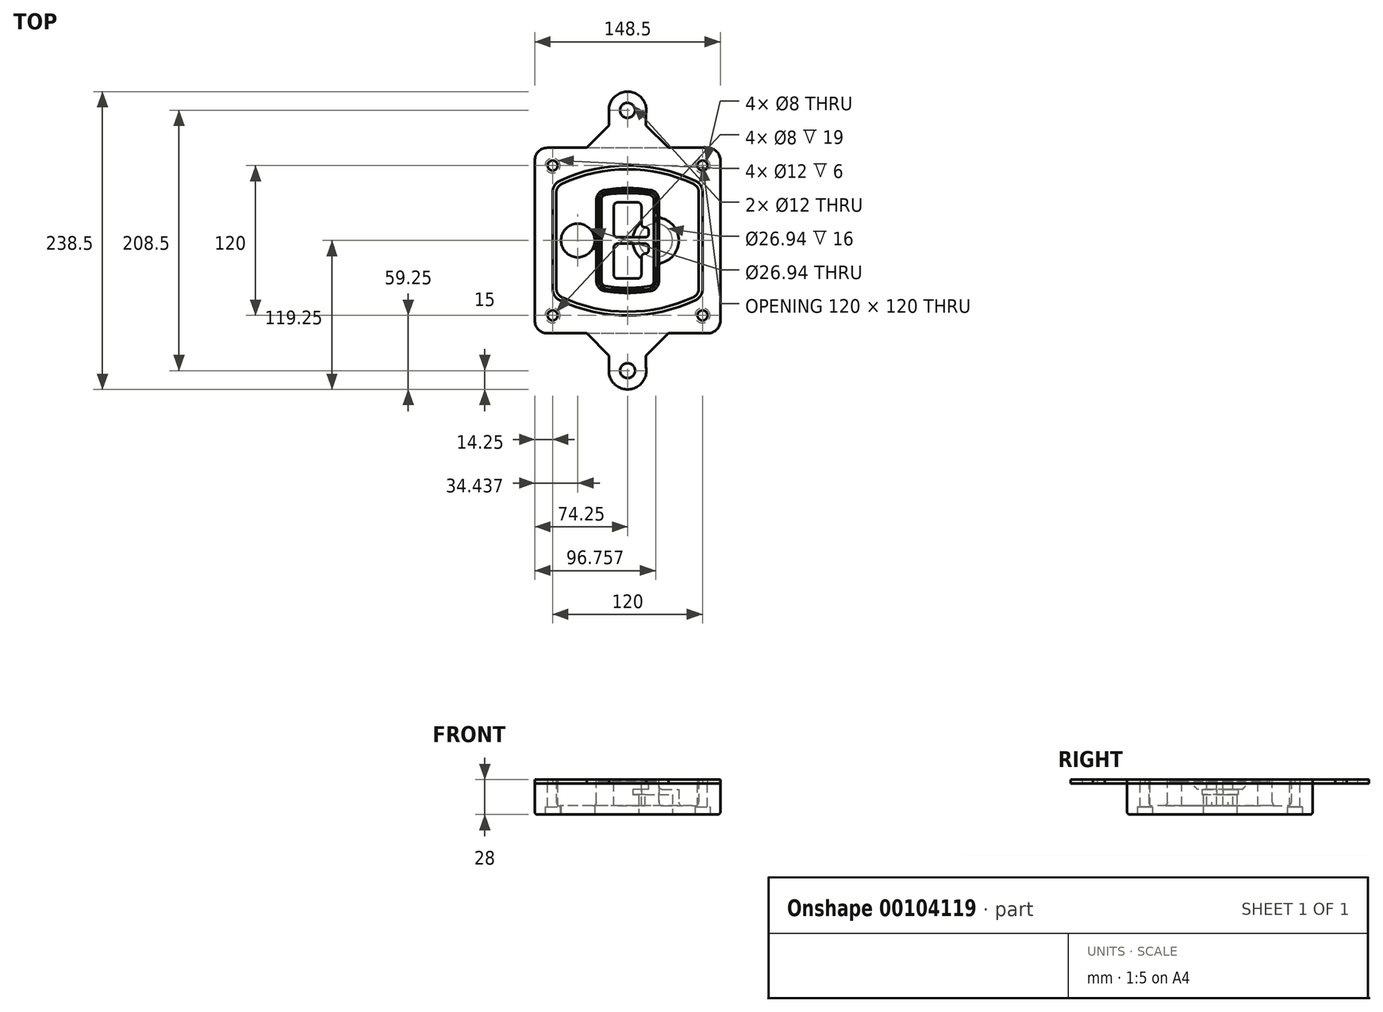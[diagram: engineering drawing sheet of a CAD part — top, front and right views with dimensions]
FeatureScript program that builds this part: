
annotation { "Feature Type Name" : "Feature", "Feature Type Description" : "" }
export const myFeature = defineFeature(function(context is Context, id is Id, definition is map)
    precondition{}
    {
        {
            var Q0;
            Q0=qCreatedBy(makeId("Top.planeOp"),FACE);
            var sketch = newSketch(context, id + "F0", { "sketchPlane" : qUnion([Q0])});
            skPoint(sketch, "E0.rect.middle", {"position": v(0, 0) * mm});
            skLineSegment(sketch, "E1.bottom", {"start": v(-64.25, -74.25) * mm, "end": v(64.25, -74.25) * mm});
            skLineSegment(sketch, "E1.top", {"start": v(-64.25, 74.25) * mm, "end": v(64.25, 74.25) * mm});
            skLineSegment(sketch, "E1.left", {"start": v(-74.25, -64.25) * mm, "end": v(-74.25, 64.25) * mm});
            skLineSegment(sketch, "E1.right", {"start": v(74.25, -64.25) * mm, "end": v(74.25, 64.25) * mm});
            skLineSegment(sketch, "E2", {"start": v(-74.25, 74.25) * mm, "end": v(74.25, -74.25) * mm, "construction": true});
            skLineSegment(sketch, "E3", {"start": v(74.25, 74.25) * mm, "end": v(-74.25, -74.25) * mm, "construction": true});
            skCircle(sketch, "E4", {"center": v(-60, 60) * mm, "radius": 4 * mm});
            skCircle(sketch, "E5", {"center": v(60, 60) * mm, "radius": 4 * mm});
            skCircle(sketch, "E6", {"center": v(60, -60) * mm, "radius": 4 * mm});
            skCircle(sketch, "E7", {"center": v(-60, -60) * mm, "radius": 4 * mm});
            skLineSegment(sketch, "E8", {"start": v(-60, 60) * mm, "end": v(60, 60) * mm, "construction": true});
            skLineSegment(sketch, "E9", {"start": v(60, 60) * mm, "end": v(60, -60) * mm, "construction": true});
            skLineSegment(sketch, "E10", {"start": v(60, -60) * mm, "end": v(-60, -60) * mm, "construction": true});
            skLineSegment(sketch, "E11", {"start": v(-60, -60) * mm, "end": v(-60, 60) * mm, "construction": true});
            skLineSegment(sketch, "E12", {"start": v(-60, 38.83) * mm, "end": v(-60, -38.83) * mm});
            skLineSegment(sketch, "E13", {"start": v(60, 38.83) * mm, "end": v(60, -38.83) * mm});
            skArc(sketch, "E14", {"start": v(54.26, 47.88) * mm, "mid": v(0, 60) * mm, "end": v(-54.26, 47.88) * mm});
            skArc(sketch, "E15", {"start": v(-54.26, -47.88) * mm, "mid": v(0, -60) * mm, "end": v(54.26, -47.88) * mm});
            skLineSegment(sketch, "E16", {"start": v(-60, 0) * mm, "end": v(60, 0) * mm, "construction": true});
            skPoint(sketch, "E17.visualSharp", {"position": v(-60, -45) * mm});
            skArc(sketch, "E17.filletArc", {"start": v(-60, -38.83) * mm, "mid": v(-58.44, -44.2) * mm, "end": v(-54.26, -47.88) * mm});
            skPoint(sketch, "E18.visualSharp", {"position": v(-60, 45) * mm});
            skArc(sketch, "E18.filletArc", {"start": v(-54.26, 47.88) * mm, "mid": v(-58.44, 44.2) * mm, "end": v(-60, 38.83) * mm});
            skPoint(sketch, "E19.visualSharp", {"position": v(60, 45) * mm});
            skArc(sketch, "E19.filletArc", {"start": v(60, 38.83) * mm, "mid": v(58.44, 44.2) * mm, "end": v(54.26, 47.88) * mm});
            skPoint(sketch, "E20.visualSharp", {"position": v(60, -45) * mm});
            skArc(sketch, "E20.filletArc", {"start": v(54.26, -47.88) * mm, "mid": v(58.44, -44.2) * mm, "end": v(60, -38.83) * mm});
            skPoint(sketch, "E21.visualSharp", {"position": v(-74.25, 74.25) * mm});
            skArc(sketch, "E21.filletArc", {"start": v(-64.25, 74.25) * mm, "mid": v(-71.32, 71.32) * mm, "end": v(-74.25, 64.25) * mm});
            skPoint(sketch, "E22.visualSharp", {"position": v(74.25, 74.25) * mm});
            skArc(sketch, "E22.filletArc", {"start": v(74.25, 64.25) * mm, "mid": v(71.32, 71.32) * mm, "end": v(64.25, 74.25) * mm});
            skPoint(sketch, "E23.visualSharp", {"position": v(74.25, -74.25) * mm});
            skArc(sketch, "E23.filletArc", {"start": v(64.25, -74.25) * mm, "mid": v(71.32, -71.32) * mm, "end": v(74.25, -64.25) * mm});
            skPoint(sketch, "E24.visualSharp", {"position": v(-74.25, -74.25) * mm});
            skArc(sketch, "E24.filletArc", {"start": v(-74.25, -64.25) * mm, "mid": v(-71.32, -71.32) * mm, "end": v(-64.25, -74.25) * mm});
            skArc(sketch, "E25.0", {"start": v(57, 38.83) * mm, "mid": v(55.9, 42.58) * mm, "end": v(52.98, 45.17) * mm});
            skLineSegment(sketch, "E25.1", {"start": v(57, 38.83) * mm, "end": v(57, -38.83) * mm});
            skArc(sketch, "E25.2", {"start": v(52.98, -45.17) * mm, "mid": v(55.9, -42.58) * mm, "end": v(57, -38.83) * mm});
            skArc(sketch, "E25.3", {"start": v(-52.98, -45.17) * mm, "mid": v(0, -57) * mm, "end": v(52.98, -45.17) * mm});
            skArc(sketch, "E25.4", {"start": v(-57, -38.83) * mm, "mid": v(-55.9, -42.58) * mm, "end": v(-52.98, -45.17) * mm});
            skArc(sketch, "E25.5", {"start": v(52.98, 45.17) * mm, "mid": v(0, 57) * mm, "end": v(-52.98, 45.17) * mm});
            skLineSegment(sketch, "E25.6", {"start": v(-57, 38.83) * mm, "end": v(-57, -38.83) * mm});
            skArc(sketch, "E25.7", {"start": v(-52.98, 45.17) * mm, "mid": v(-55.9, 42.58) * mm, "end": v(-57, 38.83) * mm});
            skArc(sketch, "E26.0", {"start": v(-55.96, 51.5) * mm, "mid": v(-61.82, 46.33) * mm, "end": v(-64, 38.83) * mm});
            skArc(sketch, "E26.1", {"start": v(55.96, 51.5) * mm, "mid": v(0, 64) * mm, "end": v(-55.96, 51.5) * mm});
            skArc(sketch, "E26.2", {"start": v(64, 38.83) * mm, "mid": v(61.82, 46.33) * mm, "end": v(55.96, 51.5) * mm});
            skLineSegment(sketch, "E26.3", {"start": v(64, 38.83) * mm, "end": v(64, -38.83) * mm});
            skArc(sketch, "E26.4", {"start": v(55.96, -51.5) * mm, "mid": v(61.82, -46.33) * mm, "end": v(64, -38.83) * mm});
            skLineSegment(sketch, "E26.5", {"start": v(-64, 38.83) * mm, "end": v(-64, -38.83) * mm});
            skArc(sketch, "E26.6", {"start": v(-55.96, -51.5) * mm, "mid": v(0, -64) * mm, "end": v(55.96, -51.5) * mm});
            skArc(sketch, "E26.7", {"start": v(-64, -38.83) * mm, "mid": v(-61.82, -46.33) * mm, "end": v(-55.96, -51.5) * mm});
            skSolve(sketch);
        }
        {
            var Q0;
            Q0=makeQuery(id+"F0.imprint","IMPRINT",FACE,{"disambiguationData":[TD([[makeQuery(id+"F0.imprint","IMPRINT",EDGE,{"derivedFrom":sQuery(id+"F0.wireOp",EDGE,"E1.bottom")}),1.0]])]});
            var Q1;
            Q1=makeQuery(id+"F0.imprint","IMPRINT",FACE,{"disambiguationData":[TD([[makeQuery(id+"F0.imprint","IMPRINT",EDGE,{"derivedFrom":sQuery(id+"F0.wireOp",EDGE,"E12")}),1.0]])]});
            var Q2;
            Q2=makeQuery(id+"F0.imprint","IMPRINT",FACE,{"disambiguationData":[TD([[makeQuery(id+"F0.imprint","IMPRINT",EDGE,{"derivedFrom":sQuery(id+"F0.wireOp",EDGE,"E25.0")}),1.0]])]});
            var Q3;
            Q3=makeQuery(id+"F0.imprint","IMPRINT",FACE,{"disambiguationData":[TD([[makeQuery(id+"F0.imprint","IMPRINT",EDGE,{"derivedFrom":sQuery(id+"F0.wireOp",EDGE,"E12")}),-1.0]])]});
            extrude(context, id + "F1", {"entities" : qUnion([Q0, Q1, Q2, Q3]), "oppositeDirection" : true, "depth" : 25 * mm});
        }
        {
            var Q0;
            Q0=makeQuery(id+"F0.imprint","IMPRINT",FACE,{"disambiguationData":[TD([[makeQuery(id+"F0.imprint","IMPRINT",EDGE,{"derivedFrom":sQuery(id+"F0.wireOp",EDGE,"E12")}),1.0]])]});
            extrude(context, id + "F2", {"entities" : qUnion([Q0]), "operationType" : NewBodyOperationType.ADD, "depth" : 3 * mm});
        }
        {
            var Q0;
            Q0=makeQuery(id+"F0.imprint","IMPRINT",FACE,{"disambiguationData":[TD([[makeQuery(id+"F0.imprint","IMPRINT",EDGE,{"derivedFrom":sQuery(id+"F0.wireOp",EDGE,"E25.0")}),1.0]])]});
            extrude(context, id + "F3", {"entities" : qUnion([Q0]), "operationType" : NewBodyOperationType.REMOVE, "oppositeDirection" : true, "depth" : 18 * mm});
        }
        {
            var Q0;
            Q0=makeQuery(id+"F2.opExtrude","CAP_FACE",FACE,{"disambiguationData":[OSD([sQuery(id+"F0.wireOp",EDGE,"E12"),sQuery(id+"F0.wireOp",EDGE,"E13"),sQuery(id+"F0.wireOp",EDGE,"E14"),sQuery(id+"F0.wireOp",EDGE,"E15"),sQuery(id+"F0.wireOp",EDGE,"E17.filletArc"),sQuery(id+"F0.wireOp",EDGE,"E18.filletArc"),sQuery(id+"F0.wireOp",EDGE,"E19.filletArc"),sQuery(id+"F0.wireOp",EDGE,"E20.filletArc"),sQuery(id+"F0.wireOp",EDGE,"E25.0"),sQuery(id+"F0.wireOp",EDGE,"E25.1"),sQuery(id+"F0.wireOp",EDGE,"E25.2"),sQuery(id+"F0.wireOp",EDGE,"E25.3"),sQuery(id+"F0.wireOp",EDGE,"E25.4"),sQuery(id+"F0.wireOp",EDGE,"E25.5"),sQuery(id+"F0.wireOp",EDGE,"E25.6"),sQuery(id+"F0.wireOp",EDGE,"E25.7")])],"isStart":false});
            var sketch = newSketch(context, id + "F4", { "sketchPlane" : qUnion([Q0])});
            skArc(sketch, "E27.0", {"start": v(-18.34, -40.45) * mm, "mid": v(0, -42) * mm, "end": v(18.34, -40.45) * mm});
            skArc(sketch, "E28.0", {"start": v(18.34, 40.45) * mm, "mid": v(0, 42) * mm, "end": v(-18.34, 40.45) * mm});
            skLineSegment(sketch, "E29", {"start": v(-25, 32.57) * mm, "end": v(-25, -32.57) * mm});
            skLineSegment(sketch, "E30", {"start": v(25, 32.57) * mm, "end": v(25, -32.57) * mm});
            skLineSegment(sketch, "E31", {"start": v(-25, 39.1) * mm, "end": v(25, 39.1) * mm, "construction": true});
            skLineSegment(sketch, "E32", {"start": v(-25, -39.1) * mm, "end": v(25, -39.1) * mm, "construction": true});
            skPoint(sketch, "E33.visualSharp", {"position": v(-25, 39.1) * mm});
            skArc(sketch, "E33.filletArc", {"start": v(-18.34, 40.45) * mm, "mid": v(-23.11, 37.73) * mm, "end": v(-25, 32.57) * mm});
            skPoint(sketch, "E34.visualSharp", {"position": v(25, 39.1) * mm});
            skArc(sketch, "E34.filletArc", {"start": v(25, 32.57) * mm, "mid": v(23.11, 37.73) * mm, "end": v(18.34, 40.45) * mm});
            skPoint(sketch, "E35.visualSharp", {"position": v(25, -39.1) * mm});
            skArc(sketch, "E35.filletArc", {"start": v(18.34, -40.45) * mm, "mid": v(23.11, -37.73) * mm, "end": v(25, -32.57) * mm});
            skPoint(sketch, "E36.visualSharp", {"position": v(-25, -39.1) * mm});
            skArc(sketch, "E36.filletArc", {"start": v(-25, -32.57) * mm, "mid": v(-23.11, -37.73) * mm, "end": v(-18.34, -40.45) * mm});
            skArc(sketch, "E37.0", {"start": v(52.98, 45.17) * mm, "mid": v(0, 57) * mm, "end": v(-52.98, 45.17) * mm});
            skArc(sketch, "E37.1", {"start": v(-52.98, 45.17) * mm, "mid": v(-55.9, 42.58) * mm, "end": v(-57, 38.83) * mm});
            skLineSegment(sketch, "E37.2", {"start": v(-57, 38.83) * mm, "end": v(-57, -38.83) * mm});
            skArc(sketch, "E37.3", {"start": v(-57, -38.83) * mm, "mid": v(-55.9, -42.58) * mm, "end": v(-52.98, -45.17) * mm});
            skArc(sketch, "E37.4", {"start": v(-52.98, -45.17) * mm, "mid": v(0, -57) * mm, "end": v(52.98, -45.17) * mm});
            skArc(sketch, "E37.5", {"start": v(52.98, -45.17) * mm, "mid": v(55.9, -42.58) * mm, "end": v(57, -38.83) * mm});
            skLineSegment(sketch, "E37.6", {"start": v(57, 38.83) * mm, "end": v(57, -38.83) * mm});
            skArc(sketch, "E37.7", {"start": v(57, 38.83) * mm, "mid": v(55.9, 42.58) * mm, "end": v(52.98, 45.17) * mm});
            skLineSegment(sketch, "E38.0", {"start": v(23, 32.57) * mm, "end": v(23, -32.57) * mm});
            skArc(sketch, "E38.1", {"start": v(18, -38.48) * mm, "mid": v(21.58, -36.44) * mm, "end": v(23, -32.57) * mm});
            skArc(sketch, "E38.2", {"start": v(-18, -38.48) * mm, "mid": v(0, -40) * mm, "end": v(18, -38.48) * mm});
            skArc(sketch, "E38.3", {"start": v(-23, -32.57) * mm, "mid": v(-21.58, -36.44) * mm, "end": v(-18, -38.48) * mm});
            skLineSegment(sketch, "E38.4", {"start": v(-23, 32.57) * mm, "end": v(-23, -32.57) * mm});
            skArc(sketch, "E38.5", {"start": v(23, 32.57) * mm, "mid": v(21.58, 36.44) * mm, "end": v(18, 38.48) * mm});
            skArc(sketch, "E38.6", {"start": v(-18, 38.48) * mm, "mid": v(-21.58, 36.44) * mm, "end": v(-23, 32.57) * mm});
            skArc(sketch, "E38.7", {"start": v(18, 38.48) * mm, "mid": v(0, 40) * mm, "end": v(-18, 38.48) * mm});
            skArc(sketch, "E39.0", {"start": v(21, 32.57) * mm, "mid": v(20.06, 35.15) * mm, "end": v(17.67, 36.5) * mm});
            skLineSegment(sketch, "E39.1", {"start": v(21, 32.57) * mm, "end": v(21, -32.57) * mm});
            skArc(sketch, "E39.2", {"start": v(17.67, -36.5) * mm, "mid": v(20.06, -35.15) * mm, "end": v(21, -32.57) * mm});
            skArc(sketch, "E39.3", {"start": v(-17.67, -36.5) * mm, "mid": v(0, -38) * mm, "end": v(17.67, -36.5) * mm});
            skArc(sketch, "E39.4", {"start": v(-21, -32.57) * mm, "mid": v(-20.06, -35.15) * mm, "end": v(-17.67, -36.5) * mm});
            skArc(sketch, "E39.5", {"start": v(17.67, 36.5) * mm, "mid": v(0, 38) * mm, "end": v(-17.67, 36.5) * mm});
            skLineSegment(sketch, "E39.6", {"start": v(-21, 32.57) * mm, "end": v(-21, -32.57) * mm});
            skArc(sketch, "E39.7", {"start": v(-17.67, 36.5) * mm, "mid": v(-20.06, 35.15) * mm, "end": v(-21, 32.57) * mm});
            skLineSegment(sketch, "E40", {"start": v(-25, 0) * mm, "end": v(25, 0) * mm, "construction": true});
            skLineSegment(sketch, "E41", {"start": v(-11, 5.5) * mm, "end": v(-11, 27.5) * mm});
            skLineSegment(sketch, "E42", {"start": v(-8, 30.5) * mm, "end": v(8, 30.5) * mm});
            skLineSegment(sketch, "E43", {"start": v(11, 27.5) * mm, "end": v(11, 13.5) * mm});
            skLineSegment(sketch, "E44", {"start": v(14, 10.5) * mm, "end": v(14, 10.5) * mm});
            skLineSegment(sketch, "E45", {"start": v(17, 7.5) * mm, "end": v(17, 5.5) * mm});
            skLineSegment(sketch, "E46", {"start": v(14, 2.5) * mm, "end": v(-8, 2.5) * mm});
            skPoint(sketch, "E47.visualSharp", {"position": v(-11, 30.5) * mm});
            skArc(sketch, "E47.filletArc", {"start": v(-8, 30.5) * mm, "mid": v(-10.12, 29.62) * mm, "end": v(-11, 27.5) * mm});
            skPoint(sketch, "E48.visualSharp", {"position": v(11, 30.5) * mm});
            skArc(sketch, "E48.filletArc", {"start": v(11, 27.5) * mm, "mid": v(10.12, 29.62) * mm, "end": v(8, 30.5) * mm});
            skPoint(sketch, "E49.visualSharp", {"position": v(11, 10.5) * mm});
            skArc(sketch, "E49.filletArc", {"start": v(11, 13.5) * mm, "mid": v(11.88, 11.38) * mm, "end": v(14, 10.5) * mm});
            skPoint(sketch, "E50.visualSharp", {"position": v(17, 10.5) * mm});
            skArc(sketch, "E50.filletArc", {"start": v(17, 7.5) * mm, "mid": v(16.12, 9.62) * mm, "end": v(14, 10.5) * mm});
            skPoint(sketch, "E51.visualSharp", {"position": v(17, 2.5) * mm});
            skArc(sketch, "E51.filletArc", {"start": v(14, 2.5) * mm, "mid": v(16.12, 3.38) * mm, "end": v(17, 5.5) * mm});
            skPoint(sketch, "E52.visualSharp", {"position": v(-11, 2.5) * mm});
            skArc(sketch, "E52.filletArc", {"start": v(-11, 5.5) * mm, "mid": v(-10.12, 3.38) * mm, "end": v(-8, 2.5) * mm});
            skLineSegment(sketch, "E53.0.MirrorCS", {"start": v(14, -2.5) * mm, "end": v(-8, -2.5) * mm});
            skArc(sketch, "E54.0.MirrorCS", {"start": v(-11, -5.5) * mm, "mid": v(-10.12, -3.38) * mm, "end": v(-8, -2.5) * mm});
            skLineSegment(sketch, "E55.0.MirrorCS", {"start": v(-11, -5.5) * mm, "end": v(-11, -27.5) * mm});
            skArc(sketch, "E56.0.MirrorCS", {"start": v(-8, -30.5) * mm, "mid": v(-10.12, -29.62) * mm, "end": v(-11, -27.5) * mm});
            skLineSegment(sketch, "E57.0.MirrorCS", {"start": v(-8, -30.5) * mm, "end": v(8, -30.5) * mm});
            skArc(sketch, "E58.0.MirrorCS", {"start": v(11, -27.5) * mm, "mid": v(10.12, -29.62) * mm, "end": v(8, -30.5) * mm});
            skLineSegment(sketch, "E59.0.MirrorCS", {"start": v(11, -27.5) * mm, "end": v(11, -13.5) * mm});
            skArc(sketch, "E60.0.MirrorCS", {"start": v(11, -13.5) * mm, "mid": v(11.88, -11.38) * mm, "end": v(14, -10.5) * mm});
            skArc(sketch, "E61.0.MirrorCS", {"start": v(17, -7.5) * mm, "mid": v(16.12, -9.62) * mm, "end": v(14, -10.5) * mm});
            skLineSegment(sketch, "E62.0.MirrorCS", {"start": v(17, -7.5) * mm, "end": v(17, -5.5) * mm});
            skArc(sketch, "E63.0.MirrorCS", {"start": v(14, -2.5) * mm, "mid": v(16.12, -3.38) * mm, "end": v(17, -5.5) * mm});
            skSolve(sketch);
        }
        {
            var Q0;
            Q0=makeQuery(id+"F4.imprint","IMPRINT",FACE,{"disambiguationData":[TD([[makeQuery(id+"F4.imprint","IMPRINT",EDGE,{"derivedFrom":sQuery(id+"F4.wireOp",EDGE,"E27.0")}),1.0]])]});
            var Q1;
            Q1=makeQuery(id+"F4.imprint","IMPRINT",FACE,{"disambiguationData":[TD([[makeQuery(id+"F4.imprint","IMPRINT",EDGE,{"derivedFrom":sQuery(id+"F4.wireOp",EDGE,"E38.0")}),-1.0]])]});
            var Q2;
            Q2=makeQuery(id+"F4.imprint","IMPRINT",FACE,{"disambiguationData":[TD([[makeQuery(id+"F4.imprint","IMPRINT",EDGE,{"derivedFrom":sQuery(id+"F4.wireOp",EDGE,"E39.0")}),1.0]])]});
            extrude(context, id + "F5", {"entities" : qUnion([Q0, Q1, Q2]), "operationType" : NewBodyOperationType.ADD, "endBound" : BoundingType.UP_TO_NEXT, "oppositeDirection" : true, "depth" : 25 * mm});
        }
        {
            var Q0;
            Q0=makeQuery(id+"F4.imprint","IMPRINT",FACE,{"disambiguationData":[TD([[makeQuery(id+"F4.imprint","IMPRINT",EDGE,{"derivedFrom":sQuery(id+"F4.wireOp",EDGE,"E38.0")}),-1.0]])]});
            extrude(context, id + "F6", {"entities" : qUnion([Q0]), "operationType" : NewBodyOperationType.REMOVE, "oppositeDirection" : true, "depth" : 2 * mm});
        }
        {
            var Q0;
            Q0=makeQuery(id+"F1.opExtrude","CAP_FACE",FACE,{"disambiguationData":[OSD([sQuery(id+"F0.wireOp",EDGE,"E1.bottom"),sQuery(id+"F0.wireOp",EDGE,"E1.top"),sQuery(id+"F0.wireOp",EDGE,"E1.left"),sQuery(id+"F0.wireOp",EDGE,"E1.right"),sQuery(id+"F0.wireOp",EDGE,"E4"),sQuery(id+"F0.wireOp",EDGE,"E5"),sQuery(id+"F0.wireOp",EDGE,"E6"),sQuery(id+"F0.wireOp",EDGE,"E7"),sQuery(id+"F0.wireOp",EDGE,"E21.filletArc"),sQuery(id+"F0.wireOp",EDGE,"E22.filletArc"),sQuery(id+"F0.wireOp",EDGE,"E23.filletArc"),sQuery(id+"F0.wireOp",EDGE,"E24.filletArc")])],"isStart":false});
            var sketch = newSketch(context, id + "F7", { "sketchPlane" : qUnion([Q0])});
            skCircle(sketch, "E64", {"center": v(22.5, 0) * mm, "radius": 13.47 * mm});
            skCircle(sketch, "E65", {"center": v(-39.81, 0) * mm, "radius": 13.47 * mm});
            skLineSegment(sketch, "E66", {"start": v(74.25, 0) * mm, "end": v(-74.25, 0) * mm});
            skCircle(sketch, "E67", {"center": v(22.5, 0) * mm, "radius": 18.47 * mm});
            skCircle(sketch, "E68", {"center": v(60, -60) * mm, "radius": 6 * mm});
            skCircle(sketch, "E69", {"center": v(-60, -60) * mm, "radius": 6 * mm});
            skCircle(sketch, "E70", {"center": v(-60, 60) * mm, "radius": 6 * mm});
            skCircle(sketch, "E71", {"center": v(60, 60) * mm, "radius": 6 * mm});
            skSolve(sketch);
        }
        {
            var Q0;
            {var subQ1=sQuery(id+"F7.wireOp",EDGE,"E66");var subQ4=sQuery(id+"F7.wireOp",EDGE,"E64");var subQ6=makeQuery(id+"F7.imprint","INTERSECT",VERTEX,{"disambiguationData":[OD(0.0)],"derivedFrom":[subQ4,subQ1]});Q0=makeQuery(id+"F7.imprint","IMPRINT",FACE,{"disambiguationData":[TD([[makeQuery(id+"F7.imprint","IMPRINT",EDGE,{"disambiguationData":[TD([[subQ6,-1.0]])],"derivedFrom":subQ4}),-1.0]])]});}
            var Q1;
            {var subQ0=sQuery(id+"F7.wireOp",EDGE,"E66");var subQ1=sQuery(id+"F7.wireOp",EDGE,"E64");var subQ3=makeQuery(id+"F7.imprint","INTERSECT",VERTEX,{"disambiguationData":[OD(0.0)],"derivedFrom":[subQ1,subQ0]});Q1=makeQuery(id+"F7.imprint","IMPRINT",FACE,{"disambiguationData":[TD([[makeQuery(id+"F7.imprint","IMPRINT",EDGE,{"disambiguationData":[TD([[subQ3,-1.0]])],"derivedFrom":subQ1}),1.0]])]});}
            var Q2;
            {var subQ0=sQuery(id+"F7.wireOp",EDGE,"E66");var subQ1=sQuery(id+"F7.wireOp",EDGE,"E64");var subQ3=makeQuery(id+"F7.imprint","INTERSECT",VERTEX,{"disambiguationData":[OD(0.0)],"derivedFrom":[subQ1,subQ0]});Q2=makeQuery(id+"F7.imprint","IMPRINT",FACE,{"disambiguationData":[TD([[makeQuery(id+"F7.imprint","IMPRINT",EDGE,{"disambiguationData":[TD([[subQ3,1.0]])],"derivedFrom":subQ1}),1.0]])]});}
            var Q3;
            {var subQ1=sQuery(id+"F7.wireOp",EDGE,"E66");var subQ4=sQuery(id+"F7.wireOp",EDGE,"E64");var subQ6=makeQuery(id+"F7.imprint","INTERSECT",VERTEX,{"disambiguationData":[OD(0.0)],"derivedFrom":[subQ4,subQ1]});Q3=makeQuery(id+"F7.imprint","IMPRINT",FACE,{"disambiguationData":[TD([[makeQuery(id+"F7.imprint","IMPRINT",EDGE,{"disambiguationData":[TD([[subQ6,1.0]])],"derivedFrom":subQ4}),-1.0]])]});}
            extrude(context, id + "F8", {"entities" : qUnion([Q0, Q1, Q2, Q3]), "operationType" : NewBodyOperationType.ADD, "oppositeDirection" : true, "depth" : 20 * mm});
        }
        {
            var Q0;
            {var subQ0=sQuery(id+"F7.wireOp",EDGE,"E66");var subQ1=sQuery(id+"F7.wireOp",EDGE,"E64");var subQ3=makeQuery(id+"F7.imprint","INTERSECT",VERTEX,{"disambiguationData":[OD(0.0)],"derivedFrom":[subQ1,subQ0]});Q0=makeQuery(id+"F7.imprint","IMPRINT",FACE,{"disambiguationData":[TD([[makeQuery(id+"F7.imprint","IMPRINT",EDGE,{"disambiguationData":[TD([[subQ3,-1.0]])],"derivedFrom":subQ1}),1.0]])]});}
            var Q1;
            {var subQ0=sQuery(id+"F7.wireOp",EDGE,"E66");var subQ1=sQuery(id+"F7.wireOp",EDGE,"E64");var subQ3=makeQuery(id+"F7.imprint","INTERSECT",VERTEX,{"disambiguationData":[OD(0.0)],"derivedFrom":[subQ1,subQ0]});Q1=makeQuery(id+"F7.imprint","IMPRINT",FACE,{"disambiguationData":[TD([[makeQuery(id+"F7.imprint","IMPRINT",EDGE,{"disambiguationData":[TD([[subQ3,1.0]])],"derivedFrom":subQ1}),1.0]])]});}
            extrude(context, id + "F9", {"entities" : qUnion([Q0, Q1]), "operationType" : NewBodyOperationType.REMOVE, "oppositeDirection" : true, "depth" : 16 * mm});
        }
        {
            var Q0;
            {var subQ0=sQuery(id+"F7.wireOp",EDGE,"E66");var subQ1=sQuery(id+"F7.wireOp",EDGE,"E65");var subQ3=makeQuery(id+"F7.imprint","INTERSECT",VERTEX,{"disambiguationData":[OD(0.0)],"derivedFrom":[subQ1,subQ0]});Q0=makeQuery(id+"F7.imprint","IMPRINT",FACE,{"disambiguationData":[TD([[makeQuery(id+"F7.imprint","IMPRINT",EDGE,{"disambiguationData":[TD([[subQ3,-1.0]])],"derivedFrom":subQ1}),1.0]])]});}
            var Q1;
            {var subQ0=sQuery(id+"F7.wireOp",EDGE,"E66");var subQ1=sQuery(id+"F7.wireOp",EDGE,"E65");var subQ3=makeQuery(id+"F7.imprint","INTERSECT",VERTEX,{"disambiguationData":[OD(0.0)],"derivedFrom":[subQ1,subQ0]});Q1=makeQuery(id+"F7.imprint","IMPRINT",FACE,{"disambiguationData":[TD([[makeQuery(id+"F7.imprint","IMPRINT",EDGE,{"disambiguationData":[TD([[subQ3,1.0]])],"derivedFrom":subQ1}),1.0]])]});}
            extrude(context, id + "F10", {"entities" : qUnion([Q0, Q1]), "operationType" : NewBodyOperationType.REMOVE, "oppositeDirection" : true, "depth" : 25 * mm});
        }
        {
            var Q0;
            Q0=makeQuery(id+"F7.imprint","IMPRINT",FACE,{"disambiguationData":[TD([[makeQuery(id+"F7.imprint","IMPRINT",EDGE,{"derivedFrom":sQuery(id+"F7.wireOp",EDGE,"E68")}),1.0]])]});
            var Q1;
            Q1=makeQuery(id+"F7.imprint","IMPRINT",FACE,{"disambiguationData":[TD([[makeQuery(id+"F7.imprint","IMPRINT",EDGE,{"derivedFrom":makeQuery(id+"F1.opExtrude","CAP_EDGE",EDGE,{"disambiguationData":[OSD([sQuery(id+"F0.wireOp",EDGE,"E5")])],"isStart":false})}),-1.0]])]});
            var Q2;
            Q2=makeQuery(id+"F7.imprint","IMPRINT",FACE,{"disambiguationData":[TD([[makeQuery(id+"F7.imprint","IMPRINT",EDGE,{"derivedFrom":sQuery(id+"F7.wireOp",EDGE,"E69")}),1.0]])]});
            var Q3;
            Q3=makeQuery(id+"F7.imprint","IMPRINT",FACE,{"disambiguationData":[TD([[makeQuery(id+"F7.imprint","IMPRINT",EDGE,{"derivedFrom":makeQuery(id+"F1.opExtrude","CAP_EDGE",EDGE,{"disambiguationData":[OSD([sQuery(id+"F0.wireOp",EDGE,"E4")])],"isStart":false})}),-1.0]])]});
            var Q4;
            Q4=makeQuery(id+"F7.imprint","IMPRINT",FACE,{"disambiguationData":[TD([[makeQuery(id+"F7.imprint","IMPRINT",EDGE,{"derivedFrom":sQuery(id+"F7.wireOp",EDGE,"E70")}),1.0]])]});
            var Q5;
            Q5=makeQuery(id+"F7.imprint","IMPRINT",FACE,{"disambiguationData":[TD([[makeQuery(id+"F7.imprint","IMPRINT",EDGE,{"derivedFrom":makeQuery(id+"F1.opExtrude","CAP_EDGE",EDGE,{"disambiguationData":[OSD([sQuery(id+"F0.wireOp",EDGE,"E7")])],"isStart":false})}),-1.0]])]});
            var Q6;
            Q6=makeQuery(id+"F7.imprint","IMPRINT",FACE,{"disambiguationData":[TD([[makeQuery(id+"F7.imprint","IMPRINT",EDGE,{"derivedFrom":sQuery(id+"F7.wireOp",EDGE,"E71")}),1.0]])]});
            var Q7;
            Q7=makeQuery(id+"F7.imprint","IMPRINT",FACE,{"disambiguationData":[TD([[makeQuery(id+"F7.imprint","IMPRINT",EDGE,{"derivedFrom":makeQuery(id+"F1.opExtrude","CAP_EDGE",EDGE,{"disambiguationData":[OSD([sQuery(id+"F0.wireOp",EDGE,"E6")])],"isStart":false})}),-1.0]])]});
            extrude(context, id + "F11", {"entities" : qUnion([Q0, Q1, Q2, Q3, Q4, Q5, Q6, Q7]), "operationType" : NewBodyOperationType.REMOVE, "oppositeDirection" : true, "depth" : 6 * mm});
        }
        {
            var Q0;
            Q0=makeQuery(id+"F9.boolean.opBoolean","COPY",FACE,{"derivedFrom":makeQuery(id+"F9.opExtrude","CAP_FACE",FACE,{"disambiguationData":[OSD([sQuery(id+"F7.wireOp",EDGE,"E64")])],"isStart":false})});
            var sketch = newSketch(context, id + "F12", { "sketchPlane" : qUnion([Q0])});
            skArc(sketch, "E72.0", {"start": v(11, 14.45) * mm, "mid": v(6.45, 9.13) * mm, "end": v(4.2, 2.5) * mm});
            skArc(sketch, "E72.1", {"start": v(4.2, -2.5) * mm, "mid": v(6.45, -9.13) * mm, "end": v(11, -14.45) * mm});
            skLineSegment(sketch, "E73", {"start": v(4.2, -2.5) * mm, "end": v(14, -2.5) * mm});
            skLineSegment(sketch, "E74.0", {"start": v(14, 2.5) * mm, "end": v(4.2, 2.5) * mm});
            skArc(sketch, "E74.1", {"start": v(14, 2.5) * mm, "mid": v(16.12, 3.38) * mm, "end": v(17, 5.5) * mm});
            skLineSegment(sketch, "E74.2", {"start": v(17, 7.5) * mm, "end": v(17, 5.5) * mm});
            skArc(sketch, "E74.3", {"start": v(17, 7.5) * mm, "mid": v(16.12, 9.62) * mm, "end": v(14, 10.5) * mm});
            skArc(sketch, "E74.4", {"start": v(11, 13.5) * mm, "mid": v(11.88, 11.38) * mm, "end": v(14, 10.5) * mm});
            skLineSegment(sketch, "E74.5", {"start": v(11, 14.45) * mm, "end": v(11, 13.5) * mm});
            skLineSegment(sketch, "E74.7", {"start": v(14, -2.5) * mm, "end": v(4.2, -2.5) * mm});
            skArc(sketch, "E74.8", {"start": v(14, -2.5) * mm, "mid": v(16.12, -3.38) * mm, "end": v(17, -5.5) * mm});
            skLineSegment(sketch, "E74.9", {"start": v(17, -7.5) * mm, "end": v(17, -5.5) * mm});
            skArc(sketch, "E74.10", {"start": v(17, -7.5) * mm, "mid": v(16.12, -9.62) * mm, "end": v(14, -10.5) * mm});
            skArc(sketch, "E74.11", {"start": v(11, -13.5) * mm, "mid": v(11.88, -11.38) * mm, "end": v(14, -10.5) * mm});
            skLineSegment(sketch, "E74.12", {"start": v(11, -14.45) * mm, "end": v(11, -13.5) * mm});
            skPoint(sketch, "E75.orphan", {"position": v(11, -27.5) * mm});
            skPoint(sketch, "E76.orphan", {"position": v(-8, -2.5) * mm});
            skPoint(sketch, "E77.orphan", {"position": v(-8, 2.5) * mm});
            skPoint(sketch, "E78.orphan", {"position": v(11, 27.5) * mm});
            skSolve(sketch);
        }
        {
            var Q0;
            {var subQ7=sQuery(id+"F12.wireOp",EDGE,"E72.0");var subQ14=sQuery(id+"F12.wireOp",EDGE,"E72.1");var subQ16=sQuery(id+"F12.wireOp",EDGE,"E74.1");var subQ18=sQuery(id+"F12.wireOp",EDGE,"E74.8");Q0=qUnion([makeQuery(id+"F12.imprint","IMPRINT",FACE,{"disambiguationData":[TD([[makeQuery(id+"F12.imprint","IMPRINT",EDGE,{"derivedFrom":subQ7}),1.0]])]}),makeQuery(id+"F12.imprint","IMPRINT",FACE,{"disambiguationData":[TD([[makeQuery(id+"F12.imprint","IMPRINT",EDGE,{"derivedFrom":subQ14}),1.0]])]}),makeQuery(id+"F12.imprint","IMPRINT",FACE,{"disambiguationData":[TD([[makeQuery(id+"F12.imprint","IMPRINT",EDGE,{"derivedFrom":subQ16}),1.0]])]}),makeQuery(id+"F12.imprint","IMPRINT",FACE,{"disambiguationData":[TD([[makeQuery(id+"F12.imprint","IMPRINT",EDGE,{"derivedFrom":subQ18}),-1.0]])]})]);}
            var Q1;
            Q1=makeQuery(id+"F5.boolean.opBoolean","SPLIT",FACE,{"disambiguationData":[TD([makeQuery(id+"F5.opExtrude","SWEPT_FACE",FACE,{"disambiguationData":[OSD([sQuery(id+"F4.wireOp",EDGE,"E41")])]})])],"derivedFrom":makeQuery(id+"F3.boolean.opBoolean","COPY",FACE,{"derivedFrom":makeQuery(id+"F3.opExtrude","CAP_FACE",FACE,{"disambiguationData":[OSD([sQuery(id+"F0.wireOp",EDGE,"E25.0"),sQuery(id+"F0.wireOp",EDGE,"E25.1"),sQuery(id+"F0.wireOp",EDGE,"E25.2"),sQuery(id+"F0.wireOp",EDGE,"E25.3"),sQuery(id+"F0.wireOp",EDGE,"E25.4"),sQuery(id+"F0.wireOp",EDGE,"E25.5"),sQuery(id+"F0.wireOp",EDGE,"E25.6"),sQuery(id+"F0.wireOp",EDGE,"E25.7")])],"isStart":false})})});
            extrude(context, id + "F13", {"entities" : qUnion([Q0]), "operationType" : NewBodyOperationType.REMOVE, "endBound" : BoundingType.UP_TO_SURFACE, "endBoundEntityFace" : qUnion([Q1]), "depth" : 25 * mm});
        }
        {
            var Q0;
            Q0=makeQuery(id+"F3.boolean.opBoolean","COPY",EDGE,{"derivedFrom":makeQuery(id+"F3.opExtrude","CAP_EDGE",EDGE,{"disambiguationData":[OSD([sQuery(id+"F0.wireOp",EDGE,"E25.6")])],"isStart":false})});
            var Q1;
            Q1=makeQuery(id+"F8.boolean.opBoolean","INTERSECT",EDGE,{"derivedFrom":[makeQuery(id+"F5.opExtrude","SWEPT_FACE",FACE,{"disambiguationData":[OSD([sQuery(id+"F4.wireOp",EDGE,"E30")])]}),makeQuery(id+"F8.opExtrude","CAP_FACE",FACE,{"disambiguationData":[OSD([sQuery(id+"F7.wireOp",EDGE,"E67")])],"isStart":false})]});
            var Q2;
            Q2=makeQuery(id+"F8.boolean.opBoolean","INTERSECT",EDGE,{"disambiguationData":[OD(1.0)],"derivedFrom":[makeQuery(id+"F5.opExtrude","SWEPT_FACE",FACE,{"disambiguationData":[OSD([sQuery(id+"F4.wireOp",EDGE,"E30")])]}),makeQuery(id+"F8.opExtrude","SWEPT_FACE",FACE,{"disambiguationData":[OSD([sQuery(id+"F7.wireOp",EDGE,"E67")])]})]});
            var Q3;
            {var subQ0=sQuery(id+"F4.wireOp",EDGE,"E30");Q3=makeQuery(id+"F8.boolean.opBoolean","SPLIT",EDGE,{"disambiguationData":[TD([makeQuery(id+"F5.opExtrude","SWEPT_FACE",FACE,{"disambiguationData":[OSD([sQuery(id+"F4.wireOp",EDGE,"E35.filletArc")])]})])],"derivedFrom":makeQuery(id+"F5.opExtrude","CAP_EDGE",EDGE,{"disambiguationData":[OSD([subQ0])],"isStart":false})});}
            var Q4;
            {var subQ0=sQuery(id+"F0.wireOp",EDGE,"E25.7");var subQ1=sQuery(id+"F0.wireOp",EDGE,"E25.1");var subQ2=sQuery(id+"F0.wireOp",EDGE,"E25.6");var subQ3=sQuery(id+"F0.wireOp",EDGE,"E25.5");var subQ4=sQuery(id+"F0.wireOp",EDGE,"E25.4");var subQ5=sQuery(id+"F0.wireOp",EDGE,"E25.0");var subQ6=sQuery(id+"F0.wireOp",EDGE,"E25.2");var subQ7=sQuery(id+"F0.wireOp",EDGE,"E25.3");Q4=makeQuery(id+"F8.boolean.opBoolean","INTERSECT",EDGE,{"derivedFrom":[makeQuery(id+"F5.boolean.opBoolean","SPLIT",FACE,{"disambiguationData":[TD([makeQuery(id+"F2.opExtrude","SWEPT_FACE",FACE,{"disambiguationData":[OSD([subQ5])]})])],"derivedFrom":makeQuery(id+"F3.boolean.opBoolean","COPY",FACE,{"derivedFrom":makeQuery(id+"F3.opExtrude","CAP_FACE",FACE,{"disambiguationData":[OSD([subQ5,subQ1,subQ6,subQ7,subQ4,subQ3,subQ2,subQ0])],"isStart":false})})}),makeQuery(id+"F8.opExtrude","SWEPT_FACE",FACE,{"disambiguationData":[OSD([sQuery(id+"F7.wireOp",EDGE,"E67")])]})]});}
            var Q5;
            Q5=makeQuery(id+"F8.boolean.opBoolean","INTERSECT",EDGE,{"disambiguationData":[OD(0.0)],"derivedFrom":[makeQuery(id+"F5.opExtrude","SWEPT_FACE",FACE,{"disambiguationData":[OSD([sQuery(id+"F4.wireOp",EDGE,"E30")])]}),makeQuery(id+"F8.opExtrude","SWEPT_FACE",FACE,{"disambiguationData":[OSD([sQuery(id+"F7.wireOp",EDGE,"E67")])]})]});
            fillet(context, id + "F14", {"entities" : qUnion([Q0, Q1, Q2, Q3, Q4, Q5]), "radius" : 3 * mm, "tangentPropagation" : true, "allowEdgeOverflow" : false});
        }
        {
            var Q0;
            Q0=makeQuery(id+"F1.opExtrude","CAP_EDGE",EDGE,{"disambiguationData":[OSD([sQuery(id+"F0.wireOp",EDGE,"E1.bottom")])],"isStart":false});
            fillet(context, id + "F15", {"entities" : qUnion([Q0]), "radius" : 2 * mm, "tangentPropagation" : true, "allowEdgeOverflow" : false});
        }
        {
            var Q0;
            {var subQ0=sQuery(id+"F0.wireOp",EDGE,"E22.filletArc");var subQ1=sQuery(id+"F0.wireOp",EDGE,"E7");var subQ2=sQuery(id+"F0.wireOp",EDGE,"E6");var subQ3=sQuery(id+"F0.wireOp",EDGE,"E5");var subQ4=sQuery(id+"F0.wireOp",EDGE,"E4");var subQ5=sQuery(id+"F0.wireOp",EDGE,"E1.bottom");var subQ6=sQuery(id+"F0.wireOp",EDGE,"E21.filletArc");var subQ7=sQuery(id+"F0.wireOp",EDGE,"E1.top");var subQ8=sQuery(id+"F0.wireOp",EDGE,"E1.left");var subQ9=sQuery(id+"F0.wireOp",EDGE,"E1.right");var subQ10=sQuery(id+"F0.wireOp",EDGE,"E23.filletArc");var subQ11=sQuery(id+"F0.wireOp",EDGE,"E24.filletArc");Q0=makeQuery(id+"F2.boolean.opBoolean","SPLIT",FACE,{"disambiguationData":[TD([makeQuery(id+"F1.opExtrude","SWEPT_FACE",FACE,{"disambiguationData":[OSD([subQ5])]})])],"derivedFrom":makeQuery(id+"F1.opExtrude","CAP_FACE",FACE,{"disambiguationData":[OSD([subQ5,subQ7,subQ8,subQ9,subQ4,subQ3,subQ2,subQ1,subQ6,subQ0,subQ10,subQ11])],"isStart":true})});}
            var sketch = newSketch(context, id + "F16", { "sketchPlane" : qUnion([Q0])});
            skLineSegment(sketch, "E79", {"start": v(0, 74.25) * mm, "end": v(0, 104.25) * mm, "construction": true});
            skLineSegment(sketch, "E80", {"start": v(-32.74, 74.25) * mm, "end": v(-14.74, 92.25) * mm});
            skLineSegment(sketch, "E81", {"start": v(-14.74, 92.25) * mm, "end": v(-14.74, 101.49) * mm});
            skArc(sketch, "E82", {"start": v(14.74, 101.49) * mm, "mid": v(0, 119.25) * mm, "end": v(-14.74, 101.49) * mm});
            skLineSegment(sketch, "E83", {"start": v(14.74, 101.49) * mm, "end": v(14.74, 92.25) * mm});
            skLineSegment(sketch, "E84", {"start": v(32.74, 74.25) * mm, "end": v(14.74, 92.25) * mm});
            skCircle(sketch, "E85", {"center": v(0, 104.25) * mm, "radius": 6 * mm});
            skLineSegment(sketch, "E86", {"start": v(0, 0) * mm, "end": v(-74.25, 0) * mm});
            skLineSegment(sketch, "E87", {"start": v(-74.25, 0) * mm, "end": v(0, 0) * mm});
            skLineSegment(sketch, "E88", {"start": v(74.25, 0) * mm, "end": v(0, 0) * mm});
            skLineSegment(sketch, "E89.MirrorCS", {"start": v(-32.74, -74.25) * mm, "end": v(-14.74, -92.25) * mm});
            skLineSegment(sketch, "E90.MirrorCS", {"start": v(-14.74, -92.25) * mm, "end": v(-14.74, -101.49) * mm});
            skArc(sketch, "E91.MirrorCS", {"start": v(14.74, -101.49) * mm, "mid": v(0, -119.25) * mm, "end": v(-14.74, -101.49) * mm});
            skLineSegment(sketch, "E92.MirrorCS", {"start": v(14.74, -101.49) * mm, "end": v(14.74, -92.25) * mm});
            skLineSegment(sketch, "E93.MirrorCS", {"start": v(32.74, -74.25) * mm, "end": v(14.74, -92.25) * mm});
            skCircle(sketch, "E94.MirrorC", {"center": v(0, -104.25) * mm, "radius": 6 * mm});
            skSolve(sketch);
        }
        {
            var Q0;
            Q0=makeQuery(id+"F16.imprint","IMPRINT",FACE,{"disambiguationData":[TD([[makeQuery(id+"F16.imprint","IMPRINT",EDGE,{"derivedFrom":makeQuery(id+"F1.opExtrude","CAP_EDGE",EDGE,{"disambiguationData":[OSD([sQuery(id+"F0.wireOp",EDGE,"E4")])],"isStart":true})}),-1.0]])]});
            var Q1;
            {var subQ0=sQuery(id+"F16.wireOp",EDGE,"E80");Q1=makeQuery(id+"F16.imprint","IMPRINT",FACE,{"disambiguationData":[TD([[makeQuery(id+"F16.imprint","IMPRINT",EDGE,{"derivedFrom":subQ0}),-1.0]])]});}
            var Q2;
            Q2=makeQuery(id+"F16.imprint","IMPRINT",FACE,{"disambiguationData":[TD([[makeQuery(id+"F16.imprint","IMPRINT",EDGE,{"derivedFrom":makeQuery(id+"F1.opExtrude","CAP_EDGE",EDGE,{"disambiguationData":[OSD([sQuery(id+"F0.wireOp",EDGE,"E6")])],"isStart":true})}),-1.0]])]});
            var Q3;
            {var subQ0=sQuery(id+"F16.wireOp",EDGE,"E89.MirrorCS");Q3=makeQuery(id+"F16.imprint","IMPRINT",FACE,{"disambiguationData":[TD([[makeQuery(id+"F16.imprint","IMPRINT",EDGE,{"derivedFrom":subQ0}),1.0]])]});}
            var Q4;
            Q4=makeQuery(id+"F2.opExtrude","CAP_FACE",FACE,{"disambiguationData":[OSD([sQuery(id+"F0.wireOp",EDGE,"E12"),sQuery(id+"F0.wireOp",EDGE,"E13"),sQuery(id+"F0.wireOp",EDGE,"E14"),sQuery(id+"F0.wireOp",EDGE,"E15"),sQuery(id+"F0.wireOp",EDGE,"E17.filletArc"),sQuery(id+"F0.wireOp",EDGE,"E18.filletArc"),sQuery(id+"F0.wireOp",EDGE,"E19.filletArc"),sQuery(id+"F0.wireOp",EDGE,"E20.filletArc"),sQuery(id+"F0.wireOp",EDGE,"E25.0"),sQuery(id+"F0.wireOp",EDGE,"E25.1"),sQuery(id+"F0.wireOp",EDGE,"E25.2"),sQuery(id+"F0.wireOp",EDGE,"E25.3"),sQuery(id+"F0.wireOp",EDGE,"E25.4"),sQuery(id+"F0.wireOp",EDGE,"E25.5"),sQuery(id+"F0.wireOp",EDGE,"E25.6"),sQuery(id+"F0.wireOp",EDGE,"E25.7")])],"isStart":false});
            extrude(context, id + "F17", {"entities" : qUnion([Q0, Q1, Q2, Q3]), "endBound" : BoundingType.UP_TO_SURFACE, "endBoundEntityFace" : qUnion([Q4]), "depth" : 25 * mm});
        }
    });
